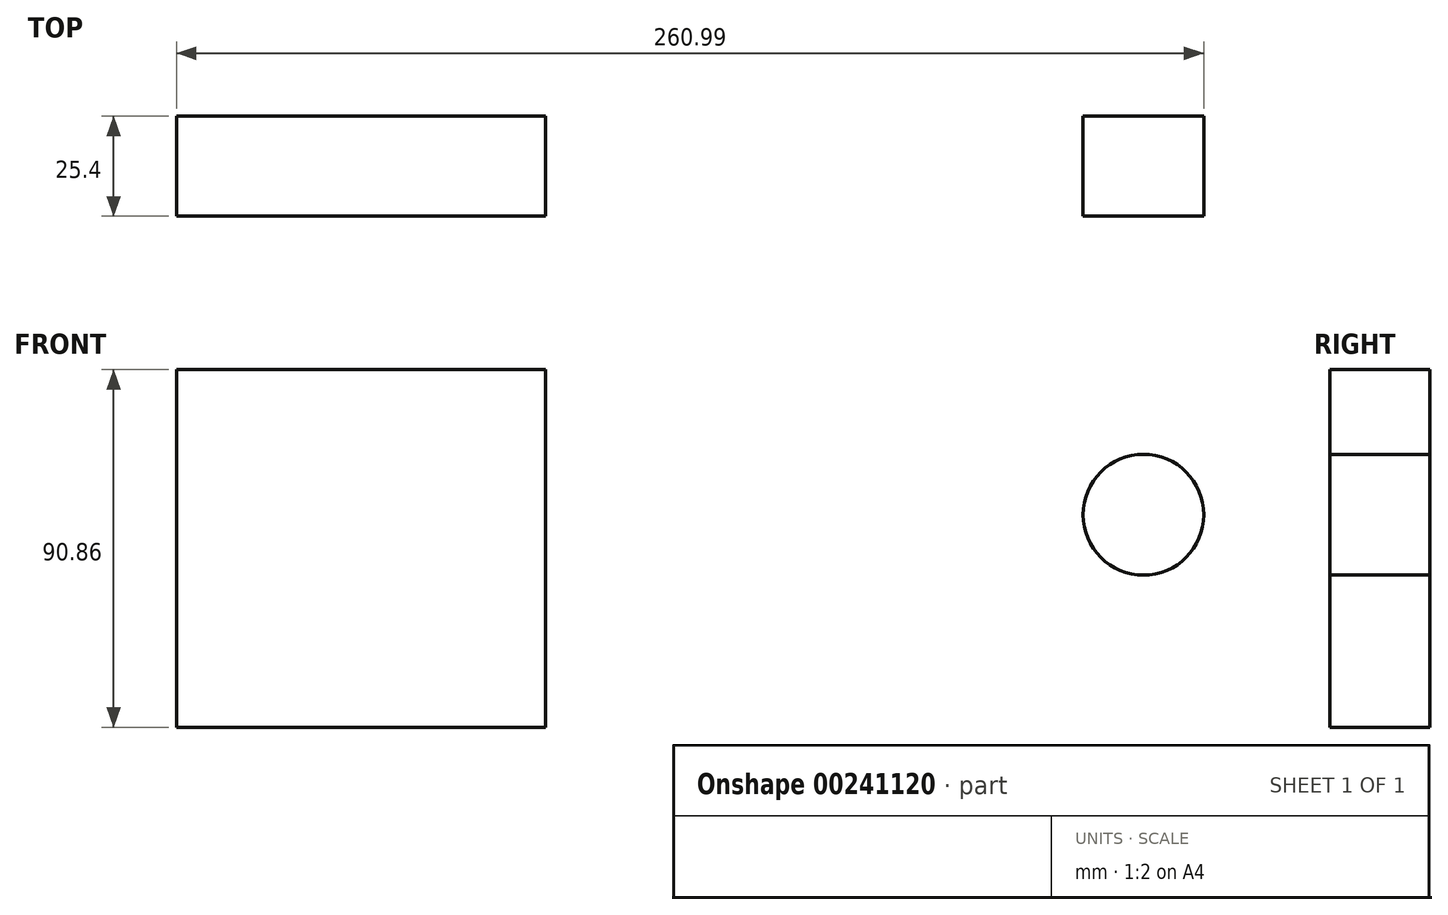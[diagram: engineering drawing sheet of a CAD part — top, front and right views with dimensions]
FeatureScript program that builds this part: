
annotation { "Feature Type Name" : "Feature", "Feature Type Description" : "" }
export const myFeature = defineFeature(function(context is Context, id is Id, definition is map)
    precondition{}
    {
        {
            var Q0;
            Q0=qCreatedBy(makeId("Front.planeOp"),FACE);
            var sketch = newSketch(context, id + "F0", { "sketchPlane" : qUnion([Q0])});
            skLineSegment(sketch, "E0.bottom", {"start": v(-9.09, 13.49) * mm, "end": v(-102.79, 13.49) * mm});
            skLineSegment(sketch, "E0.top", {"start": v(-9.09, 104.35) * mm, "end": v(-102.79, 104.35) * mm});
            skLineSegment(sketch, "E0.left", {"start": v(-9.09, 13.49) * mm, "end": v(-9.09, 104.35) * mm});
            skLineSegment(sketch, "E0.right", {"start": v(-102.79, 13.49) * mm, "end": v(-102.79, 104.35) * mm});
            skPoint(sketch, "E0.middle", {"position": v(-55.94, 58.92) * mm});
            skSolve(sketch);
        }
        {
            var Q0;
            Q0 = qSketchRegion(id + "F0", true);
            extrude(context, id + "F1", {"entities" : qUnion([Q0]), "depth" : 25.4 * mm});
        }
        {
            var Q0;
            Q0=qCreatedBy(makeId("Front.planeOp"),FACE);
            var sketch = newSketch(context, id + "F2", { "sketchPlane" : qUnion([Q0])});
            skCircle(sketch, "E1", {"center": v(142.88, 67.5) * mm, "radius": 15.33 * mm});
            skSolve(sketch);
        }
        {
            var Q0;
            Q0 = qSketchRegion(id + "F2", true);
            extrude(context, id + "F3", {"entities" : qUnion([Q0]), "depth" : 25.4 * mm});
        }
    });
